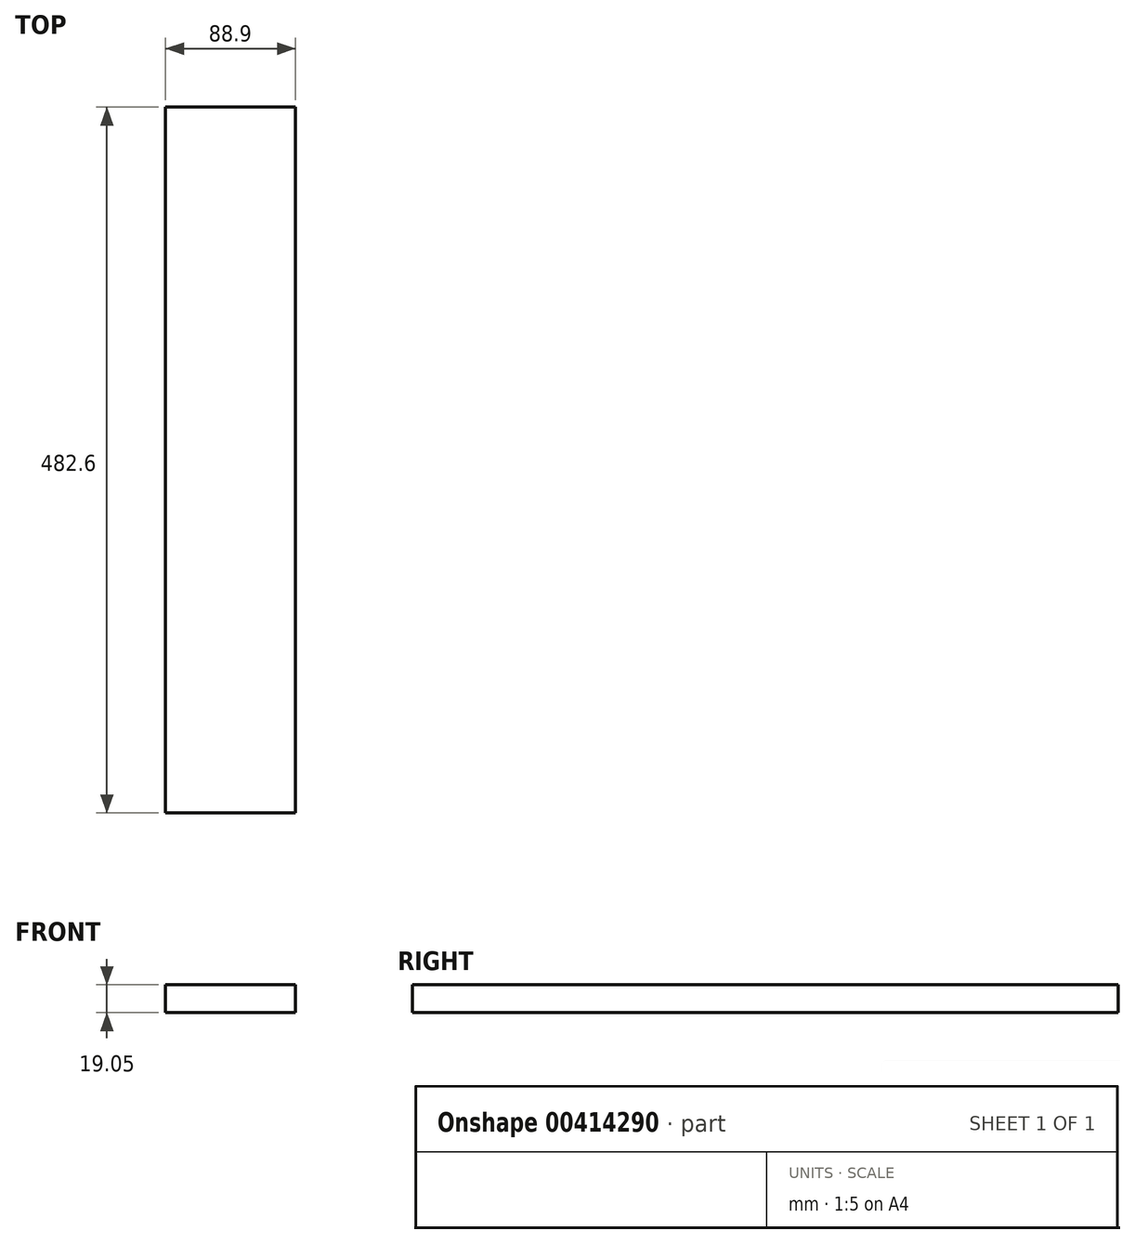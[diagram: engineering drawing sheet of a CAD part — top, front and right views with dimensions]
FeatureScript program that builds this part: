
annotation { "Feature Type Name" : "Feature", "Feature Type Description" : "" }
export const myFeature = defineFeature(function(context is Context, id is Id, definition is map)
    precondition{}
    {
        {
            var Q0;
            Q0=qCreatedBy(makeId("Front.planeOp"),FACE);
            var sketch = newSketch(context, id + "F0", { "sketchPlane" : qUnion([Q0])});
            skLineSegment(sketch, "E0.bottom", {"start": v(0, 0) * mm, "end": v(-88.9, 0) * mm});
            skLineSegment(sketch, "E0.top", {"start": v(0, 19.05) * mm, "end": v(-88.9, 19.05) * mm});
            skLineSegment(sketch, "E0.left", {"start": v(0, 0) * mm, "end": v(0, 19.05) * mm});
            skLineSegment(sketch, "E0.right", {"start": v(-88.9, 0) * mm, "end": v(-88.9, 19.05) * mm});
            skSolve(sketch);
        }
        {
            var Q0;
            Q0=qSketchRegion(id+"F0",true);
            extrude(context, id + "F1", {"entities" : qUnion([Q0]), "depth" : 482.6 * mm});
        }
    });
